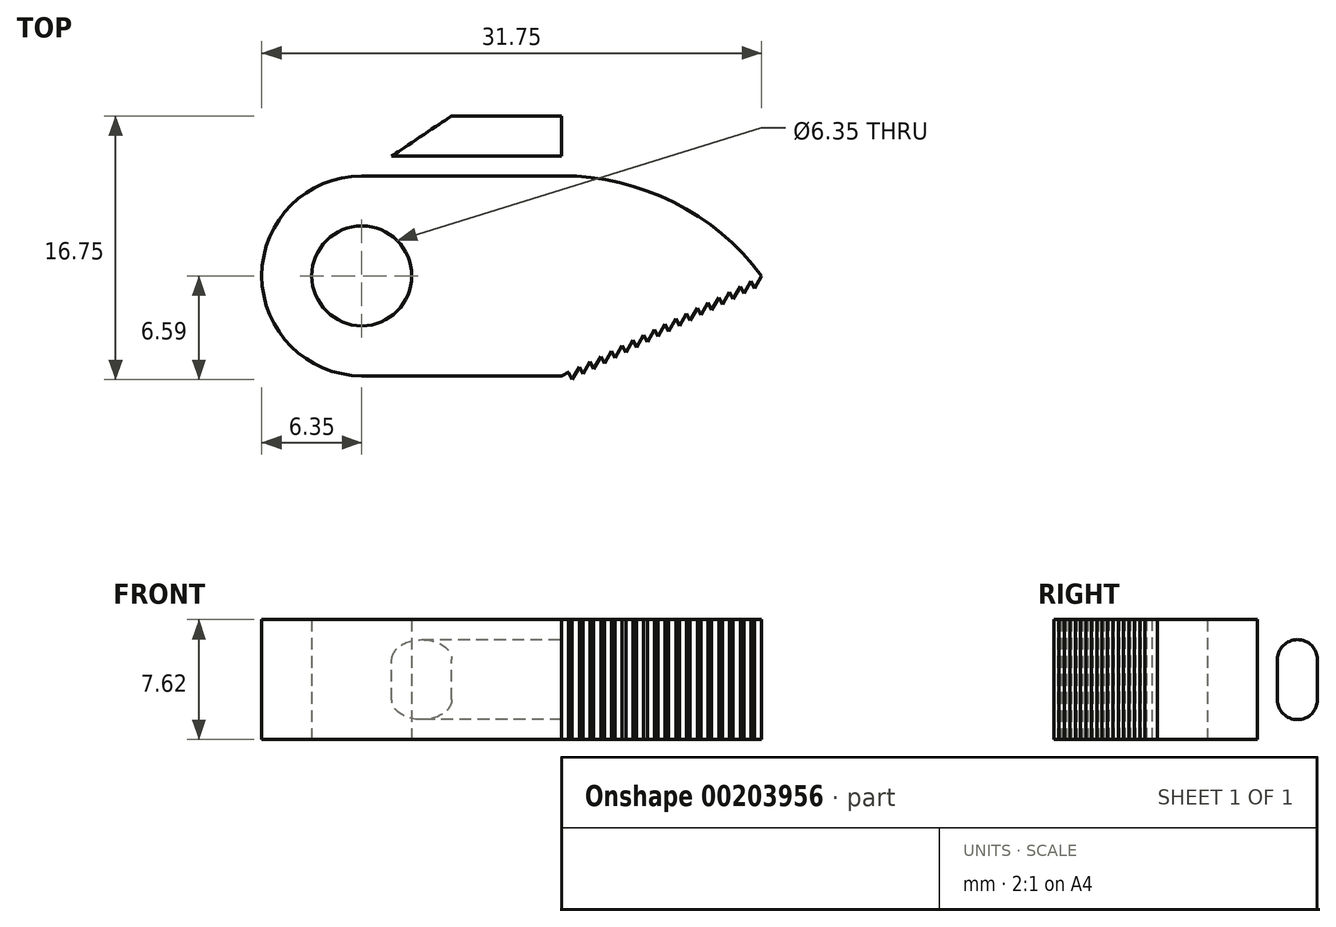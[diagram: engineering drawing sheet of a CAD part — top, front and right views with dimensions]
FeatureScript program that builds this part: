
annotation { "Feature Type Name" : "Feature", "Feature Type Description" : "" }
export const myFeature = defineFeature(function(context is Context, id is Id, definition is map)
    precondition{}
    {
        {
            var Q0;
            Q0=qCreatedBy(makeId("Top.planeOp"),FACE);
            var sketch = newSketch(context, id + "F0", { "sketchPlane" : qUnion([Q0])});
            skLineSegment(sketch, "E0", {"start": v(0, 0) * mm, "end": v(-25.4, 0) * mm});
            skCircle(sketch, "E1", {"center": v(-25.4, 0) * mm, "radius": 6.35 * mm});
            skCircle(sketch, "E2", {"center": v(-25.4, 0) * mm, "radius": 3.18 * mm});
            skLineSegment(sketch, "E3", {"start": v(-25.4, 0) * mm, "end": v(-12.7, 0) * mm});
            skLineSegment(sketch, "E4", {"start": v(-25.4, 0) * mm, "end": v(-25.4, 6.35) * mm});
            skLineSegment(sketch, "E5", {"start": v(-12.7, 0) * mm, "end": v(-12.7, 6.35) * mm});
            skLineSegment(sketch, "E6", {"start": v(-12.7, 6.35) * mm, "end": v(-25.4, 6.35) * mm});
            skLineSegment(sketch, "E7", {"start": v(-25.4, 0) * mm, "end": v(-25.4, -6.35) * mm});
            skLineSegment(sketch, "E8", {"start": v(-12.7, 0) * mm, "end": v(-12.7, -6.35) * mm});
            skLineSegment(sketch, "E9", {"start": v(-12.7, -6.35) * mm, "end": v(-25.4, -6.35) * mm});
            skArc(sketch, "E10", {"start": v(0, 0) * mm, "mid": v(-5.6, 4.67) * mm, "end": v(-12.7, 6.35) * mm});
            skLineSegment(sketch, "E11", {"start": v(0, 0) * mm, "end": v(-12.7, -6.35) * mm});
            skLineSegment(sketch, "E12", {"start": v(0, 0) * mm, "end": v(-0.45, -0.8) * mm});
            skLineSegment(sketch, "E13", {"start": v(-0.45, -0.8) * mm, "end": v(-0.68, -0.34) * mm});
            skLineSegment(sketch, "E14", {"start": v(-0.68, -0.34) * mm, "end": v(0, 0) * mm});
            skLineSegment(sketch, "E15.1.0.0", {"start": v(-0.68, -0.34) * mm, "end": v(-1.14, -1.14) * mm});
            skLineSegment(sketch, "E15.1.0.1", {"start": v(-1.14, -1.14) * mm, "end": v(-1.36, -0.68) * mm});
            skLineSegment(sketch, "E15.2.0.0", {"start": v(-1.36, -0.68) * mm, "end": v(-1.82, -1.48) * mm});
            skLineSegment(sketch, "E15.2.0.1", {"start": v(-1.82, -1.48) * mm, "end": v(-2.04, -1.02) * mm});
            skLineSegment(sketch, "E15.3.0.0", {"start": v(-2.04, -1.02) * mm, "end": v(-2.5, -1.82) * mm});
            skLineSegment(sketch, "E15.3.0.1", {"start": v(-2.5, -1.82) * mm, "end": v(-2.73, -1.36) * mm});
            skLineSegment(sketch, "E15.4.0.0", {"start": v(-2.73, -1.36) * mm, "end": v(-3.18, -2.16) * mm});
            skLineSegment(sketch, "E15.4.0.1", {"start": v(-3.18, -2.16) * mm, "end": v(-3.4, -1.7) * mm});
            skLineSegment(sketch, "E15.5.0.0", {"start": v(-3.4, -1.7) * mm, "end": v(-3.86, -2.5) * mm});
            skLineSegment(sketch, "E15.5.0.1", {"start": v(-3.86, -2.5) * mm, "end": v(-4.09, -2.05) * mm});
            skLineSegment(sketch, "E15.6.0.0", {"start": v(-4.09, -2.05) * mm, "end": v(-4.54, -2.84) * mm});
            skLineSegment(sketch, "E15.6.0.1", {"start": v(-4.54, -2.84) * mm, "end": v(-4.77, -2.39) * mm});
            skLineSegment(sketch, "E15.7.0.0", {"start": v(-4.77, -2.39) * mm, "end": v(-5.22, -3.18) * mm});
            skLineSegment(sketch, "E15.7.0.1", {"start": v(-5.22, -3.18) * mm, "end": v(-5.45, -2.73) * mm});
            skLineSegment(sketch, "E15.8.0.0", {"start": v(-5.45, -2.73) * mm, "end": v(-5.9, -3.52) * mm});
            skLineSegment(sketch, "E15.8.0.1", {"start": v(-5.9, -3.52) * mm, "end": v(-6.13, -3.07) * mm});
            skLineSegment(sketch, "E15.9.0.0", {"start": v(-6.13, -3.07) * mm, "end": v(-6.59, -3.86) * mm});
            skLineSegment(sketch, "E15.9.0.1", {"start": v(-6.59, -3.86) * mm, "end": v(-6.82, -3.4) * mm});
            skLineSegment(sketch, "E15.direction1", {"start": v(-0.45, -0.8) * mm, "end": v(-1.14, -1.14) * mm, "construction": true});
            skLineSegment(sketch, "E16.1.0.0", {"start": v(-7.27, -4.2) * mm, "end": v(-7.5, -3.75) * mm});
            skLineSegment(sketch, "E16.1.0.1", {"start": v(-6.81, -3.4) * mm, "end": v(-7.27, -4.2) * mm});
            skLineSegment(sketch, "E16.2.0.0", {"start": v(-7.95, -4.55) * mm, "end": v(-8.18, -4.1) * mm});
            skLineSegment(sketch, "E16.2.0.1", {"start": v(-7.5, -3.75) * mm, "end": v(-7.95, -4.55) * mm});
            skLineSegment(sketch, "E16.3.0.0", {"start": v(-8.63, -4.89) * mm, "end": v(-8.86, -4.43) * mm});
            skLineSegment(sketch, "E16.3.0.1", {"start": v(-8.18, -4.1) * mm, "end": v(-8.63, -4.89) * mm});
            skLineSegment(sketch, "E16.4.0.0", {"start": v(-9.31, -5.23) * mm, "end": v(-9.54, -4.77) * mm});
            skLineSegment(sketch, "E16.4.0.1", {"start": v(-8.86, -4.43) * mm, "end": v(-9.31, -5.23) * mm});
            skLineSegment(sketch, "E16.5.0.0", {"start": v(-10, -5.57) * mm, "end": v(-10.22, -5.11) * mm});
            skLineSegment(sketch, "E16.5.0.1", {"start": v(-9.54, -4.77) * mm, "end": v(-10, -5.57) * mm});
            skLineSegment(sketch, "E16.6.0.0", {"start": v(-10.68, -5.9) * mm, "end": v(-10.9, -5.45) * mm});
            skLineSegment(sketch, "E16.6.0.1", {"start": v(-10.22, -5.11) * mm, "end": v(-10.68, -5.9) * mm});
            skLineSegment(sketch, "E16.7.0.0", {"start": v(-11.36, -6.25) * mm, "end": v(-11.59, -5.8) * mm});
            skLineSegment(sketch, "E16.7.0.1", {"start": v(-10.9, -5.45) * mm, "end": v(-11.36, -6.25) * mm});
            skLineSegment(sketch, "E16.8.0.0", {"start": v(-12.04, -6.6) * mm, "end": v(-12.27, -6.14) * mm});
            skLineSegment(sketch, "E16.8.0.1", {"start": v(-11.59, -5.8) * mm, "end": v(-12.04, -6.6) * mm});
            skLineSegment(sketch, "E16.direction1", {"start": v(-6.59, -3.86) * mm, "end": v(-7.27, -4.2) * mm, "construction": true});
            skLineSegment(sketch, "E17", {"start": v(-12.27, -6.14) * mm, "end": v(-11.59, -5.8) * mm});
            skLineSegment(sketch, "E18", {"start": v(-12.27, -6.14) * mm, "end": v(-1.38, 0.56) * mm});
            skLineSegment(sketch, "E19", {"start": v(-1.38, 0.56) * mm, "end": v(0, 0) * mm});
            skSolve(sketch);
        }
        {
            var Q0;
            Q0 = qSketchRegion(id + "F0", true);
            extrude(context, id + "F1", {"entities" : qUnion([Q0]), "depth" : 7.62 * mm});
        }
        {
            var Q0;
            Q0=makeQuery(id+"F1.opExtrude","CAP_FACE",FACE,{"disambiguationData":[OSD([sQuery(id+"F0.wireOp",EDGE,"E1"),sQuery(id+"F0.wireOp",EDGE,"E2"),sQuery(id+"F0.wireOp",EDGE,"E6"),sQuery(id+"F0.wireOp",EDGE,"E9"),sQuery(id+"F0.wireOp",EDGE,"E10"),sQuery(id+"F0.wireOp",EDGE,"E11"),sQuery(id+"F0.wireOp",EDGE,"E12"),sQuery(id+"F0.wireOp",EDGE,"E13"),sQuery(id+"F0.wireOp",EDGE,"E15.1.0.0"),sQuery(id+"F0.wireOp",EDGE,"E15.1.0.1"),sQuery(id+"F0.wireOp",EDGE,"E15.2.0.0"),sQuery(id+"F0.wireOp",EDGE,"E15.2.0.1"),sQuery(id+"F0.wireOp",EDGE,"E15.3.0.0"),sQuery(id+"F0.wireOp",EDGE,"E15.3.0.1"),sQuery(id+"F0.wireOp",EDGE,"E15.4.0.0"),sQuery(id+"F0.wireOp",EDGE,"E15.4.0.1"),sQuery(id+"F0.wireOp",EDGE,"E15.5.0.0"),sQuery(id+"F0.wireOp",EDGE,"E15.5.0.1"),sQuery(id+"F0.wireOp",EDGE,"E15.6.0.0"),sQuery(id+"F0.wireOp",EDGE,"E15.6.0.1"),sQuery(id+"F0.wireOp",EDGE,"E15.7.0.0"),sQuery(id+"F0.wireOp",EDGE,"E15.7.0.1"),sQuery(id+"F0.wireOp",EDGE,"E15.8.0.0"),sQuery(id+"F0.wireOp",EDGE,"E15.8.0.1"),sQuery(id+"F0.wireOp",EDGE,"E15.9.0.0"),sQuery(id+"F0.wireOp",EDGE,"E15.9.0.1"),sQuery(id+"F0.wireOp",EDGE,"E16.1.0.0"),sQuery(id+"F0.wireOp",EDGE,"E16.1.0.1"),sQuery(id+"F0.wireOp",EDGE,"E16.2.0.0"),sQuery(id+"F0.wireOp",EDGE,"E16.2.0.1"),sQuery(id+"F0.wireOp",EDGE,"E16.3.0.0"),sQuery(id+"F0.wireOp",EDGE,"E16.3.0.1"),sQuery(id+"F0.wireOp",EDGE,"E16.4.0.0"),sQuery(id+"F0.wireOp",EDGE,"E16.4.0.1"),sQuery(id+"F0.wireOp",EDGE,"E16.5.0.0"),sQuery(id+"F0.wireOp",EDGE,"E16.5.0.1"),sQuery(id+"F0.wireOp",EDGE,"E16.6.0.0"),sQuery(id+"F0.wireOp",EDGE,"E16.6.0.1"),sQuery(id+"F0.wireOp",EDGE,"E16.7.0.0"),sQuery(id+"F0.wireOp",EDGE,"E16.7.0.1"),sQuery(id+"F0.wireOp",EDGE,"E16.8.0.0"),sQuery(id+"F0.wireOp",EDGE,"E16.8.0.1"),sQuery(id+"F0.wireOp",EDGE,"E18")])],"isStart":false});
            var sketch = newSketch(context, id + "F2", { "sketchPlane" : qUnion([Q0])});
            skLineSegment(sketch, "E20.bottom", {"start": v(-12.7, 6.35) * mm, "end": v(-25.4, 6.35) * mm});
            skLineSegment(sketch, "E20.top", {"start": v(-12.7, 11.43) * mm, "end": v(-25.4, 11.43) * mm});
            skLineSegment(sketch, "E20.left", {"start": v(-12.7, 6.35) * mm, "end": v(-12.7, 11.43) * mm});
            skLineSegment(sketch, "E20.right", {"start": v(-25.4, 6.35) * mm, "end": v(-25.4, 11.43) * mm});
            skLineSegment(sketch, "E21", {"start": v(-12.7, 11.43) * mm, "end": v(-17.78, 11.43) * mm});
            skLineSegment(sketch, "E22", {"start": v(-17.78, 11.43) * mm, "end": v(-25.4, 6.35) * mm});
            skSolve(sketch);
        }
        {
            var Q0;
            Q0=makeQuery(id+"F2.imprint","IMPRINT",FACE,{"disambiguationData":[TD([[makeQuery(id+"F2.imprint","IMPRINT",EDGE,{"derivedFrom":sQuery(id+"F2.wireOp",EDGE,"E20.bottom")}),-1.0]])]});
            extrude(context, id + "F3", {"entities" : qUnion([Q0]), "oppositeDirection" : true, "depth" : 7.62 * mm});
        }
        {
            var Q0;
            Q0=makeQuery(id+"F3.opExtrude","SWEPT_FACE",FACE,{"disambiguationData":[OSD([sQuery(id+"F2.wireOp",EDGE,"E20.left")])]});
            var sketch = newSketch(context, id + "F4", { "sketchPlane" : qUnion([Q0])});
            skLineSegment(sketch, "E23", {"start": v(6.35, 3.81) * mm, "end": v(11.43, 3.81) * mm});
            skLineSegment(sketch, "E24", {"start": v(11.43, 3.81) * mm, "end": v(10.16, 3.81) * mm});
            skLineSegment(sketch, "E25", {"start": v(6.35, 3.81) * mm, "end": v(7.62, 3.81) * mm});
            skLineSegment(sketch, "E26", {"start": v(7.62, 3.81) * mm, "end": v(7.62, 1.27) * mm});
            skLineSegment(sketch, "E27", {"start": v(10.16, 3.81) * mm, "end": v(10.16, 6.35) * mm});
            skLineSegment(sketch, "E28.bottom", {"start": v(10.16, 6.35) * mm, "end": v(7.62, 6.35) * mm});
            skLineSegment(sketch, "E28.top", {"start": v(10.16, 1.27) * mm, "end": v(7.62, 1.27) * mm});
            skLineSegment(sketch, "E28.left", {"start": v(10.16, 6.35) * mm, "end": v(10.16, 1.27) * mm});
            skLineSegment(sketch, "E28.right", {"start": v(7.62, 6.35) * mm, "end": v(7.62, 1.27) * mm});
            skSolve(sketch);
        }
        {
            var Q0;
            {var subQ0=sQuery(id+"F4.wireOp",EDGE,"E23");Q0=makeQuery(id+"F4.imprint","IMPRINT",FACE,{"disambiguationData":[TD([[makeQuery(id+"F4.imprint","IMPRINT",EDGE,{"derivedFrom":subQ0}),-1.0]])]});}
            var Q1;
            {var subQ0=sQuery(id+"F4.wireOp",EDGE,"E23");Q1=makeQuery(id+"F4.imprint","IMPRINT",FACE,{"disambiguationData":[TD([[makeQuery(id+"F4.imprint","IMPRINT",EDGE,{"derivedFrom":subQ0}),1.0]])]});}
            extrude(context, id + "F5", {"entities" : qUnion([Q0, Q1]), "operationType" : NewBodyOperationType.REMOVE, "oppositeDirection" : true, "depth" : 25.4 * mm});
        }
        {
            var Q0;
            Q0=makeQuery(id+"F1.opExtrude","SWEPT_EDGE",EDGE,{"disambiguationData":[OSD([sQuery(id+"F0.wireOp",EDGE,"E5"),sQuery(id+"F0.wireOp",EDGE,"E6"),sQuery(id+"F0.wireOp",EDGE,"E10")])]});
            var Q1;
            Q1=makeQuery(id+"F5.boolean.opBoolean","COPY",EDGE,{"derivedFrom":makeQuery(id+"F5.opExtrude","SWEPT_EDGE",EDGE,{"disambiguationData":[OSD([sQuery(id+"F4.wireOp",EDGE,"E28.top"),sQuery(id+"F4.wireOp",EDGE,"E28.right")])]})});
            var Q2;
            Q2=makeQuery(id+"F5.boolean.opBoolean","COPY",EDGE,{"derivedFrom":makeQuery(id+"F5.opExtrude","SWEPT_EDGE",EDGE,{"disambiguationData":[OSD([sQuery(id+"F4.wireOp",EDGE,"E28.bottom"),sQuery(id+"F4.wireOp",EDGE,"E28.right")])]})});
            var Q3;
            Q3=makeQuery(id+"F5.boolean.opBoolean","COPY",EDGE,{"derivedFrom":makeQuery(id+"F5.opExtrude","SWEPT_EDGE",EDGE,{"disambiguationData":[OSD([sQuery(id+"F4.wireOp",EDGE,"E28.bottom"),sQuery(id+"F4.wireOp",EDGE,"E28.left")])]})});
            var Q4;
            Q4=makeQuery(id+"F5.boolean.opBoolean","COPY",EDGE,{"derivedFrom":makeQuery(id+"F5.opExtrude","SWEPT_EDGE",EDGE,{"disambiguationData":[OSD([sQuery(id+"F4.wireOp",EDGE,"E28.top"),sQuery(id+"F4.wireOp",EDGE,"E28.left")])]})});
            fillet(context, id + "F6", {"entities" : qUnion([Q0, Q1, Q2, Q3, Q4]), "radius" : 1.27 * mm, "tangentPropagation" : true, "allowEdgeOverflow" : false});
        }
    });
